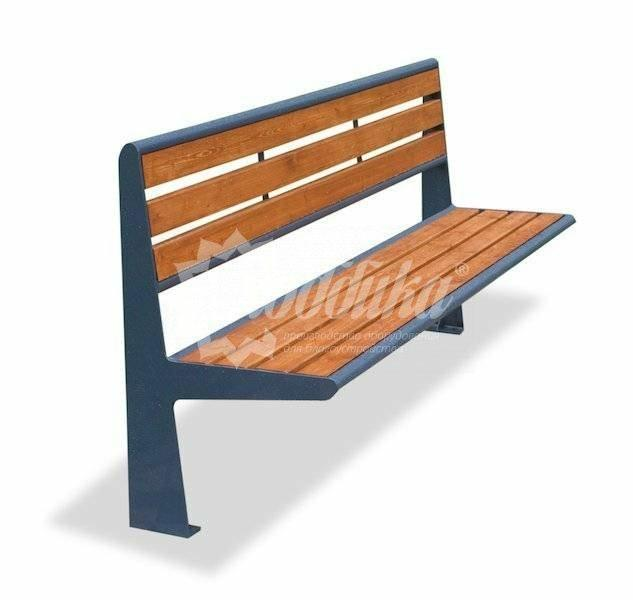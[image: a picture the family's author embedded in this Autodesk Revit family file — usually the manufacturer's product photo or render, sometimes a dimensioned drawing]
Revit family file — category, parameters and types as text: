
# Revit family: Скамейка стальная «Поло» Арт 9469
name_source: partatom
category: Антураж
revit_build: Autodesk Revit 2018 (Build: 20180423_1000(x64)
units: mm (PartAtom-declared; Revit-internal decimal feet)

## family parameters
Всегда вертикально = Да
Источник визуального образа = Геометрия семейства
На основе рабочей плоскости = Нет
Общий = Нет
При загрузке вырезать с полостями = Нет
Точка расчета площади = Нет

## types (4) — shared parameters
URL = https://hobbyka.ru
Артикул товара = Арт. 9469
Высота = 900 мм
Группа модели = Скамейки
Изготовитель = ООО «Хоббика»
Изображение типоразмера = Скамейка стальная «Поло» Арт 9469.jpg
Материал изделия = Сталь, дерево
Цвет лавки = Дерево
Цвет опор = Сталь
Ширина = 530 мм

## per-type parameters (varying)
| type | Версия 0,6 м (кресло) | Версия 1,2 м | Версия 1,8 м | Версия 2,0 м | Длина | Описание |
| Версия 0,6 м (кресло) | Да | Нет | Нет | Нет | 600 мм | Скамейка стальная «Поло». Версия 0,6 м (кресло) |
| Версия 1,2 м | Нет | Да | Нет | Нет | 1200 мм | Скамейка стальная «Поло». Версия 1,2 м |
| Версия 1,8 м | Нет | Нет | Да | Нет | 1800 мм | Скамейка стальная «Поло». Версия 1,8 м |
| Версия 2,0 м | Нет | Нет | Нет | Да | 2000 мм | Скамейка стальная «Поло». Версия 2,0 м |
